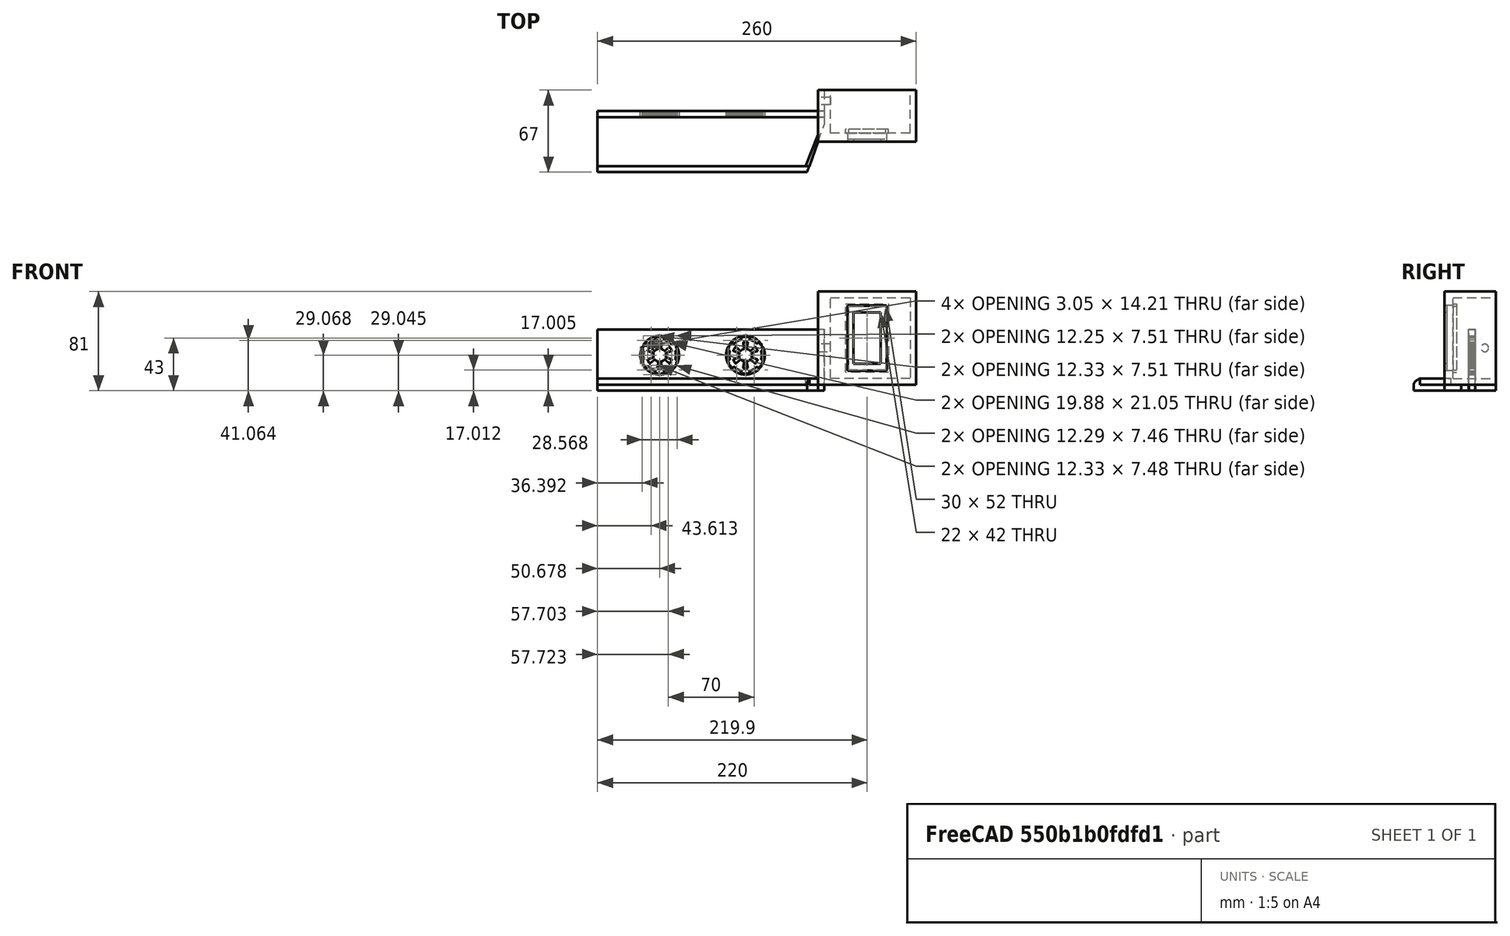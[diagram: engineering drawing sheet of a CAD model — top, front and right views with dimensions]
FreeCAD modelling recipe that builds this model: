
FCSTD DOCUMENT  (FreeCAD 1.0R39109 (Git))
Label: PC Power Button
License: All rights reserved
LicenseURL: https://en.wikipedia.org/wiki/All_rights_reserved
objects: Sketcher::SketchObject×13, PartDesign::Pad×9, PartDesign::Pocket×4, PartDesign::Body×3, Mesh::Feature×1
note: 68 computed .brp shape members not serialized (recipe doc carries the construction recipe); baked Part::Feature solids carry a one-line shape summary decoded from their .brp

FEATURE [Sketcher::SketchObject] Sketch
  ArcFitTolerance = 1e-06
  AttachmentSupport = -> [XZ_Plane]
  FullyConstrained = true
  MakeInternals = false
  MapMode = 5
  Placement = pos=(0,0,0) rot=(1,0,0;1.5708rad)
  sketch-geometry (8):
    g0: LineSegment StartX=-40 StartY=0 StartZ=0 EndX=40 EndY=0 EndZ=0
    g1: LineSegment StartX=40 StartY=0 StartZ=0 EndX=40 EndY=76 EndZ=0
    g2: LineSegment StartX=40 StartY=76 StartZ=0 EndX=-40 EndY=76 EndZ=0
    g3: LineSegment StartX=-40 StartY=76 StartZ=0 EndX=-40 EndY=0 EndZ=0
    g4: LineSegment StartX=-16.1 StartY=64.75 StartZ=0 EndX=-16.1 EndY=11.25 EndZ=0
    g5: LineSegment StartX=-16.1 StartY=11.25 StartZ=0 EndX=15.9 EndY=11.25 EndZ=0
    g6: LineSegment StartX=15.9 StartY=11.25 StartZ=0 EndX=15.9 EndY=64.75 EndZ=0
    g7: LineSegment StartX=15.9 StartY=64.75 StartZ=0 EndX=-16.1 EndY=64.75 EndZ=0
  constraints (24):
    c: Coincident(g0,g1)
    c: Coincident(g1,g2)
    c: Coincident(g2,g3)
    c: Coincident(g3,g0)
    c: Horizontal(g0)
    c: Horizontal(g2)
    c: Vertical(g1)
    c: Vertical(g3)
    c: Distance(g1,g3) = 80
    c: Distance(g0,g2) = 76
    c: PointOnObject(g0,g-1)
    c: Distance(g0,g-2) = 40
    c: Coincident(g4,g5)
    c: Coincident(g5,g6)
    c: Coincident(g6,g7)
    c: Coincident(g7,g4)
    c: Vertical(g4)
    c: Vertical(g6)
    c: Horizontal(g5)
    c: Horizontal(g7)
    c: Distance(g4,g6) = 32
    c: Distance(g5,g7) = 53.5
    c: Distance(g0,g5) = 11.25
    c: Distance(g4,g-2) = 16.1
FEATURE [PartDesign::Pad] Pad
  Direction = (0,-1,2e-16)
  Length = 7
  Length2 = 10
  Placement = pos=(0,0,0) rot=(1,0,0;1.5708rad)
  Profile = -> Sketch
  ReferenceAxis = -> Sketch [N_Axis]
  Refine = true
  Suppressed = false
  Type = 0
FEATURE [Sketcher::SketchObject] Sketch001
  ArcFitTolerance = 1e-06
  AttachmentSupport = -> [Pad]
  FullyConstrained = true
  MakeInternals = false
  MapMode = 5
  Placement = pos=(0,8.4e-15,0) rot=(-1,0,0;1.5708rad)
  sketch-geometry (8):
    g0: LineSegment StartX=-40 StartY=0 StartZ=0 EndX=-40 EndY=-76 EndZ=0
    g1: LineSegment StartX=-40 StartY=-76 StartZ=0 EndX=40 EndY=-76 EndZ=0
    g2: LineSegment StartX=40 StartY=-76 StartZ=0 EndX=40 EndY=0 EndZ=0
    g3: LineSegment StartX=40 StartY=0 StartZ=0 EndX=-40 EndY=0 EndZ=0
    g4: LineSegment StartX=-30 StartY=-5 StartZ=0 EndX=-30 EndY=-71 EndZ=0
    g5: LineSegment StartX=-30 StartY=-71 StartZ=0 EndX=35 EndY=-71 EndZ=0
    g6: LineSegment StartX=35 StartY=-71 StartZ=0 EndX=35 EndY=-5 EndZ=0
    g7: LineSegment StartX=35 StartY=-5 StartZ=0 EndX=-30 EndY=-5 EndZ=0
  constraints (24):
    c: Coincident(g0,g1)
    c: Coincident(g1,g2)
    c: Coincident(g2,g3)
    c: Coincident(g3,g0)
    c: Vertical(g0)
    c: Vertical(g2)
    c: Horizontal(g1)
    c: Horizontal(g3)
    c: Distance(g0,g2) = 80
    c: Distance(g1,g3) = 76
    c: PointOnObject(g0,g-1)
    c: Coincident(g4,g5)
    c: Coincident(g5,g6)
    c: Coincident(g6,g7)
    c: Coincident(g7,g4)
    c: Vertical(g4)
    c: Vertical(g6)
    c: Horizontal(g5)
    c: Horizontal(g7)
    c: Distance(g4,g6) = 65
    c: Distance(g5,g7) = 66
    c: Distance(g5,g1) = 5
    c: Distance(g5,g2) = 5
    c: Distance(g4,g-2) = 30
FEATURE [PartDesign::Pad] Pad001
  BaseFeature = -> Pad
  Direction = (0,1,2e-16)
  Length = 35
  Length2 = 10
  Placement = pos=(0,0,0) rot=(1,0,0;1.5708rad)
  Profile = -> Sketch001
  ReferenceAxis = -> Sketch001 [N_Axis]
  Refine = true
  Suppressed = false
  Type = 0
FEATURE [Mesh::Feature] pc_power_button  label="bticino power button socket"
  Placement = pos=(0,-9.5,-0.5) rot=(0,0,1;0rad)
FEATURE [Sketcher::SketchObject] Sketch002
  ArcFitTolerance = 1e-06
  AttachmentSupport = -> [XZ_Plane001]
  FullyConstrained = true
  MakeInternals = false
  MapMode = 5
  Placement = pos=(0,0,0) rot=(1,0,0;1.5708rad)
  sketch-geometry (8):
    g0: LineSegment StartX=-15.75 StartY=24.5 StartZ=0 EndX=-15.75 EndY=-28.5 EndZ=0
    g1: LineSegment StartX=-15.75 StartY=-28.5 StartZ=0 EndX=15.75 EndY=-28.5 EndZ=0
    g2: LineSegment StartX=15.75 StartY=-28.5 StartZ=0 EndX=15.75 EndY=24.5 EndZ=0
    g3: LineSegment StartX=15.75 StartY=24.5 StartZ=0 EndX=-15.75 EndY=24.5 EndZ=0
    g4: LineSegment StartX=-11 StartY=19 StartZ=0 EndX=-11 EndY=-23 EndZ=0
    g5: LineSegment StartX=-11 StartY=-23 StartZ=0 EndX=11 EndY=-23 EndZ=0
    g6: LineSegment StartX=11 StartY=-23 StartZ=0 EndX=11 EndY=19 EndZ=0
    g7: LineSegment StartX=11 StartY=19 StartZ=0 EndX=-11 EndY=19 EndZ=0
  constraints (24):
    c: Coincident(g0,g1)
    c: Coincident(g1,g2)
    c: Coincident(g2,g3)
    c: Coincident(g3,g0)
    c: Vertical(g0)
    c: Vertical(g2)
    c: Horizontal(g1)
    c: Horizontal(g3)
    c: Distance(g0,g2) = 31.5
    c: Distance(g1,g3) = 53
    c: DistanceY(g-1,g0) = 24.5
    c: Coincident(g4,g5)
    c: Coincident(g5,g6)
    c: Coincident(g6,g7)
    c: Coincident(g7,g4)
    c: Vertical(g4)
    c: Vertical(g6)
    c: Horizontal(g5)
    c: Horizontal(g7)
    c: Distance(g4,g6) = 22
    c: Distance(g5,g7) = 42
    c: Distance(g4,g-2) = 11
    c: Distance(g0,g-2) = 15.75
    c: Distance(g4,g-1) = 19
FEATURE [PartDesign::Pad] Pad002
  Direction = (0,-1,2e-16)
  Length = 2
  Length2 = 10
  Placement = pos=(0,0,0) rot=(1,0,0;1.5708rad)
  Profile = -> Sketch002
  ReferenceAxis = -> Sketch002 [N_Axis]
  Refine = true
  Suppressed = false
  Type = 0
FEATURE [PartDesign::Body] Body001  label="Button cover"
  AllowCompound = false
  Group = -> [Sketch002,Pad002]
  Origin = -> Origin001
  Placement = pos=(-0.1,-48,40) rot=(0,0,1;0rad)
  Tip = -> Pad002
FEATURE [Sketcher::SketchObject] Sketch003
  ArcFitTolerance = 1e-06
  AttachmentSupport = -> [XY_Plane002]
  FullyConstrained = true
  MakeInternals = false
  MapMode = 5
  sketch-geometry (5):
    g0: LineSegment StartX=0 StartY=0 StartZ=0 EndX=-9.09925 EndY=-25 EndZ=0
    g1: LineSegment StartX=0 StartY=0 StartZ=0 EndX=0 EndY=25 EndZ=0
    g2: LineSegment StartX=0 StartY=25 StartZ=0 EndX=-180 EndY=25 EndZ=0
    g3: LineSegment StartX=-180 StartY=25 StartZ=0 EndX=-180 EndY=-25 EndZ=0
    g4: LineSegment StartX=-180 StartY=-25 StartZ=0 EndX=-9.09925 EndY=-25 EndZ=0
  constraints (14):
    c: Angle(g-1,g0) = -1.91986
    c: Coincident(g0,g-1)
    c: Coincident(g1,g0)
    c: PointOnObject(g1,g-2)
    c: Distance(g2) = 180
    c: Coincident(g2,g1)
    c: Horizontal(g2)
    c: Distance(g3) = 50
    c: Coincident(g3,g2)
    c: Vertical(g3)
    c: Parallel(g4,g-1)
    c: Coincident(g3,g4)
    c: Coincident(g0,g4)
    c: DistanceY(g-1,g2) = 25
FEATURE [PartDesign::Pad] Pad003
  Direction = (0,0,1)
  Length = 5
  Length2 = 10
  Profile = -> Sketch003
  ReferenceAxis = -> Sketch003 [N_Axis]
  Refine = true
  Suppressed = false
  Type = 0
FEATURE [Sketcher::SketchObject] Sketch004
  ArcFitTolerance = 1e-06
  AttachmentSupport = -> [Pad003]
  FullyConstrained = true
  MakeInternals = false
  MapMode = 5
  Placement = pos=(-180,0,0) rot=(0.57735,-0.57735,-0.57735;2.0944rad)
  sketch-geometry (9):
    g0: LineSegment StartX=25 StartY=5 StartZ=0 EndX=20 EndY=5 EndZ=0
    g1: LineSegment StartX=20 StartY=5 StartZ=0 EndX=20 EndY=10 EndZ=0
    g2-g5: Circle [constr] x4 (B-spline internal-alignment scaffolding for g6; pole/knot coordinates omitted)
    g6: BSplineCurve PolesCount=4 KnotsCount=2 Degree=3 IsPeriodic=0
    g7: GeomPoint [constr] X=25 Y=5 Z=0
    g8: GeomPoint [constr] X=20 Y=10 Z=0
  constraints (20):
    c: Distance(g0) = 5
    c: Horizontal(g0)
    c: Distance(g0,g-1) = 5
    c: DistanceX(g-1,g0) = 20
    c: Distance(g1) = 5
    c: Parallel(g1,g-2)
    c: Coincident(g0,g1)
    c: Weight(g2) = 1
    c: Equal(g2,g3)
    c: Equal(g2,g4)
    c: Equal(g2,g5)
    c: InternalAlignment(g2-g5 -> g6) x4
    c: InternalAlignment(g7,g6)
    c: InternalAlignment(g8,g6)
    c: Coincident(g2,g0)
    c: Coincident(g1,g6)
    c: DistanceX(g1,g4) = 1.4
    c: Distance(g4,g-1) = 23.3
    c: Distance(g3,g-1) = 26
    c: DistanceX(g4,g3) = 3.4
FEATURE [PartDesign::Pad] Pad004
  BaseFeature = -> Pad003
  Direction = (-1,0,0)
  Length = 10
  Length2 = 10
  Profile = -> Sketch004
  ReferenceAxis = -> Sketch004 [N_Axis]
  Refine = true
  Reversed = true
  Suppressed = false
  Type = 3
  UpToFace = -> Pad003 [Face1]
FEATURE [Sketcher::SketchObject] Sketch005
  ArcFitTolerance = 1e-06
  AttachmentSupport = -> [Pad001]
  FullyConstrained = true
  MakeInternals = false
  MapMode = 5
  Placement = pos=(0,0,1.6e-15) rot=(1,0,0;3.14159rad)
  sketch-geometry (4):
    g0: LineSegment StartX=-40 StartY=-35 StartZ=0 EndX=-40 EndY=7 EndZ=0
    g1: LineSegment StartX=-40 StartY=-35 StartZ=0 EndX=-35 EndY=-35 EndZ=0
    g2: LineSegment StartX=-35 StartY=-35 StartZ=0 EndX=-35 EndY=-6.75 EndZ=0
    g3: LineSegment StartX=-40 StartY=7 StartZ=0 EndX=-35 EndY=-6.75 EndZ=0
  constraints (12):
    c: Distance(g0) = 42
    c: Vertical(g0)
    c: Distance(g1) = 5
    c: Coincident(g1,g0)
    c: Horizontal(g1)
    c: Distance(g2) = 28.25
    c: Coincident(g2,g1)
    c: Vertical(g2)
    c: Coincident(g2,g3)
    c: Coincident(g0,g3)
    c: DistanceX(g0,g-1) = 40
    c: Distance(g0,g-1) = 7
FEATURE [PartDesign::Pad] Pad005
  BaseFeature = -> Pad001
  Direction = (0,0,-1)
  Length = 5
  Length2 = 10
  Placement = pos=(0,0,0) rot=(1,0,0;1.5708rad)
  Profile = -> Sketch005
  ReferenceAxis = -> Sketch005 [N_Axis]
  Refine = true
  Suppressed = false
  Type = 0
FEATURE [Sketcher::SketchObject] Sketch007
  ArcFitTolerance = 1e-06
  AttachmentSupport = -> [Pad004]
  FullyConstrained = true
  MakeInternals = false
  MapMode = 5
  Placement = pos=(0,0,5) rot=(0,0,1;0rad)
  sketch-geometry (4):
    g0: LineSegment StartX=-7.25 StartY=-20 StartZ=0 EndX=-10.25 EndY=-20 EndZ=0
    g1: LineSegment StartX=-10.25 StartY=-20 StartZ=0 EndX=0 EndY=5.45 EndZ=0
    g2: LineSegment StartX=0 StartY=5.45 StartZ=0 EndX=-9e-16 EndY=0 EndZ=0
    g3: LineSegment StartX=-7.25 StartY=-20 StartZ=0 EndX=-9e-16 EndY=0 EndZ=0
  constraints (11):
    c: Distance(g0) = 3
    c: Horizontal(g0)
    c: Distance(g0,g-1) = 20
    c: Coincident(g1,g0)
    c: PointOnObject(g1,g-2)
    c: Coincident(g1,g2)
    c: Coincident(g-1,g2)
    c: Distance(g0,g-2) = 7.25
    c: DistanceY(g-1,g1) = 5.45
    c: Coincident(g3,g0)
    c: Coincident(g3,g2)
FEATURE [PartDesign::Pad] Pad006
  BaseFeature = -> Pad004
  Direction = (0,0,1)
  Length = 5
  Length2 = 10
  Profile = -> Sketch007
  ReferenceAxis = -> Sketch007 [N_Axis]
  Refine = true
  Suppressed = false
  Type = 0
FEATURE [Sketcher::SketchObject] Sketch008
  ArcFitTolerance = 1e-06
  AttachmentSupport = -> [Pad005]
  FullyConstrained = true
  MakeInternals = false
  MapMode = 5
  Placement = pos=(-40,0,0) rot=(0.707107,0,-0.707107;3.14159rad)
  sketch-geometry (4):
    g0: LineSegment StartX=5 StartY=-18.15 StartZ=0 EndX=5 EndY=-12.85 EndZ=0
    g1: LineSegment StartX=5 StartY=-12.85 StartZ=0 EndX=-45.2 EndY=-12.85 EndZ=0
    g2: LineSegment StartX=-45.2 StartY=-12.85 StartZ=0 EndX=-45.2 EndY=-18.15 EndZ=0
    g3: LineSegment StartX=-45.2 StartY=-18.15 StartZ=0 EndX=5 EndY=-18.15 EndZ=0
  constraints (12):
    c: Coincident(g0,g1)
    c: Coincident(g1,g2)
    c: Coincident(g2,g3)
    c: Coincident(g3,g0)
    c: Vertical(g0)
    c: Vertical(g2)
    c: Horizontal(g1)
    c: Horizontal(g3)
    c: Distance(g0,g2) = 50.2
    c: Distance(g1,g3) = 5.3
    c: Distance(g0,g-2) = 5
    c: Distance(g0,g-1) = 12.85
FEATURE [PartDesign::Pocket] Pocket
  BaseFeature = -> Pad005
  Direction = (1,0,2e-16)
  Length = 5
  Length2 = 5
  Placement = pos=(0,0,0) rot=(1,0,0;1.5708rad)
  Profile = -> Sketch008
  ReferenceAxis = -> Sketch008 [N_Axis]
  Refine = true
  Suppressed = false
  Type = 0
FEATURE [Sketcher::SketchObject] Sketch009
  ArcFitTolerance = 1e-06
  AttachmentSupport = -> [Pad006]
  FullyConstrained = true
  MakeInternals = false
  MapMode = 5
  Placement = pos=(0,0,0) rot=(1,0,0;3.14159rad)
  sketch-geometry (4):
    g0: LineSegment StartX=-180 StartY=-20 StartZ=0 EndX=-180 EndY=-25 EndZ=0
    g1: LineSegment StartX=-180 StartY=-25 StartZ=0 EndX=5 EndY=-25 EndZ=0
    g2: LineSegment StartX=5 StartY=-25 StartZ=0 EndX=5 EndY=-20 EndZ=0
    g3: LineSegment StartX=5 StartY=-20 StartZ=0 EndX=-180 EndY=-20 EndZ=0
  constraints (12):
    c: Coincident(g0,g1)
    c: Coincident(g1,g2)
    c: Coincident(g2,g3)
    c: Coincident(g3,g0)
    c: Vertical(g0)
    c: Vertical(g2)
    c: Horizontal(g1)
    c: Horizontal(g3)
    c: Distance(g0,g2) = 185
    c: Distance(g1,g3) = 5
    c: Distance(g0,g-1) = 20
    c: Distance(g2,g-2) = 5
FEATURE [PartDesign::Pad] Pad007
  BaseFeature = -> Pad006
  Direction = (0,0,-1)
  Length = 50
  Length2 = 10
  Profile = -> Sketch009
  ReferenceAxis = -> Sketch009 [N_Axis]
  Refine = true
  Reversed = true
  Suppressed = false
  Type = 0
FEATURE [Sketcher::SketchObject] Sketch010
  ArcFitTolerance = 1e-06
  AttachmentSupport = -> [Pad007]
  FullyConstrained = false
  MakeInternals = false
  MapMode = 5
  Placement = pos=(0,20,0) rot=(1,0,0;1.5708rad)
  sketch-geometry (176):
    g0: BSplineCurve PolesCount=4 KnotsCount=2 Degree=3 IsPeriodic=0
    g1: BSplineCurve PolesCount=4 KnotsCount=2 Degree=3 IsPeriodic=0
    g2: BSplineCurve PolesCount=4 KnotsCount=2 Degree=3 IsPeriodic=0
    g3: BSplineCurve PolesCount=4 KnotsCount=2 Degree=3 IsPeriodic=0
    g4: BSplineCurve PolesCount=4 KnotsCount=2 Degree=3 IsPeriodic=0
    g5: BSplineCurve PolesCount=4 KnotsCount=2 Degree=3 IsPeriodic=0
    g6: BSplineCurve PolesCount=4 KnotsCount=2 Degree=3 IsPeriodic=0
    g7: BSplineCurve PolesCount=4 KnotsCount=2 Degree=3 IsPeriodic=0
    g8: BSplineCurve PolesCount=4 KnotsCount=2 Degree=3 IsPeriodic=0
    g9: BSplineCurve PolesCount=4 KnotsCount=2 Degree=3 IsPeriodic=0
    g10: BSplineCurve PolesCount=4 KnotsCount=2 Degree=3 IsPeriodic=0
    g11: BSplineCurve PolesCount=4 KnotsCount=2 Degree=3 IsPeriodic=0
    g12: BSplineCurve PolesCount=4 KnotsCount=2 Degree=3 IsPeriodic=0
    g13: BSplineCurve PolesCount=4 KnotsCount=2 Degree=3 IsPeriodic=0
    g14: BSplineCurve PolesCount=4 KnotsCount=2 Degree=3 IsPeriodic=0
    g15: BSplineCurve PolesCount=4 KnotsCount=2 Degree=3 IsPeriodic=0
    g16: BSplineCurve PolesCount=4 KnotsCount=2 Degree=3 IsPeriodic=0
    g17: BSplineCurve PolesCount=4 KnotsCount=2 Degree=3 IsPeriodic=0
    g18: BSplineCurve PolesCount=4 KnotsCount=2 Degree=3 IsPeriodic=0
    g19: BSplineCurve PolesCount=4 KnotsCount=2 Degree=3 IsPeriodic=0
    g20: BSplineCurve PolesCount=4 KnotsCount=2 Degree=3 IsPeriodic=0
    g21: BSplineCurve PolesCount=4 KnotsCount=2 Degree=3 IsPeriodic=0
    g22: BSplineCurve PolesCount=4 KnotsCount=2 Degree=3 IsPeriodic=0
    g23: BSplineCurve PolesCount=4 KnotsCount=2 Degree=3 IsPeriodic=0
    g24: BSplineCurve PolesCount=4 KnotsCount=2 Degree=3 IsPeriodic=0
    g25: BSplineCurve PolesCount=4 KnotsCount=2 Degree=3 IsPeriodic=0
    g26: BSplineCurve PolesCount=4 KnotsCount=2 Degree=3 IsPeriodic=0
    g27: BSplineCurve PolesCount=4 KnotsCount=2 Degree=3 IsPeriodic=0
    g28: BSplineCurve PolesCount=4 KnotsCount=2 Degree=3 IsPeriodic=0
    g29: BSplineCurve PolesCount=4 KnotsCount=2 Degree=3 IsPeriodic=0
    g30: BSplineCurve PolesCount=4 KnotsCount=2 Degree=3 IsPeriodic=0
    g31: BSplineCurve PolesCount=4 KnotsCount=2 Degree=3 IsPeriodic=0
    g32: BSplineCurve PolesCount=4 KnotsCount=2 Degree=3 IsPeriodic=0
    g33: BSplineCurve PolesCount=4 KnotsCount=2 Degree=3 IsPeriodic=0
    g34: BSplineCurve PolesCount=4 KnotsCount=2 Degree=3 IsPeriodic=0
    g35: BSplineCurve PolesCount=4 KnotsCount=2 Degree=3 IsPeriodic=0
    g36: BSplineCurve PolesCount=4 KnotsCount=2 Degree=3 IsPeriodic=0
    g37: BSplineCurve PolesCount=4 KnotsCount=2 Degree=3 IsPeriodic=0
    g38: BSplineCurve PolesCount=4 KnotsCount=2 Degree=3 IsPeriodic=0
    g39: BSplineCurve PolesCount=4 KnotsCount=2 Degree=3 IsPeriodic=0
    g40: BSplineCurve PolesCount=4 KnotsCount=2 Degree=3 IsPeriodic=0
    g41: BSplineCurve PolesCount=4 KnotsCount=2 Degree=3 IsPeriodic=0
    g42: BSplineCurve PolesCount=4 KnotsCount=2 Degree=3 IsPeriodic=0
    g43: BSplineCurve PolesCount=4 KnotsCount=2 Degree=3 IsPeriodic=0
    g44: BSplineCurve PolesCount=4 KnotsCount=2 Degree=3 IsPeriodic=0
    g45: BSplineCurve PolesCount=4 KnotsCount=2 Degree=3 IsPeriodic=0
    g46: BSplineCurve PolesCount=4 KnotsCount=2 Degree=3 IsPeriodic=0
    g47: BSplineCurve PolesCount=4 KnotsCount=2 Degree=3 IsPeriodic=0
    g48: BSplineCurve PolesCount=4 KnotsCount=2 Degree=3 IsPeriodic=0
    g49: BSplineCurve PolesCount=4 KnotsCount=2 Degree=3 IsPeriodic=0
    g50: BSplineCurve PolesCount=4 KnotsCount=2 Degree=3 IsPeriodic=0
    g51: BSplineCurve PolesCount=4 KnotsCount=2 Degree=3 IsPeriodic=0
    g52: BSplineCurve PolesCount=4 KnotsCount=2 Degree=3 IsPeriodic=0
    g53: BSplineCurve PolesCount=4 KnotsCount=2 Degree=3 IsPeriodic=0
    g54: BSplineCurve PolesCount=4 KnotsCount=2 Degree=3 IsPeriodic=0
    g55: BSplineCurve PolesCount=4 KnotsCount=2 Degree=3 IsPeriodic=0
    g56: BSplineCurve PolesCount=4 KnotsCount=2 Degree=3 IsPeriodic=0
    g57: BSplineCurve PolesCount=4 KnotsCount=2 Degree=3 IsPeriodic=0
    g58: BSplineCurve PolesCount=4 KnotsCount=2 Degree=3 IsPeriodic=0
    g59: BSplineCurve PolesCount=4 KnotsCount=2 Degree=3 IsPeriodic=0
    g60: BSplineCurve PolesCount=4 KnotsCount=2 Degree=3 IsPeriodic=0
    g61: BSplineCurve PolesCount=4 KnotsCount=2 Degree=3 IsPeriodic=0
    g62: BSplineCurve PolesCount=4 KnotsCount=2 Degree=3 IsPeriodic=0
    g63: BSplineCurve PolesCount=4 KnotsCount=2 Degree=3 IsPeriodic=0
    g64: BSplineCurve PolesCount=4 KnotsCount=2 Degree=3 IsPeriodic=0
    g65: BSplineCurve PolesCount=4 KnotsCount=2 Degree=3 IsPeriodic=0
    g66: BSplineCurve PolesCount=4 KnotsCount=2 Degree=3 IsPeriodic=0
    g67: BSplineCurve PolesCount=4 KnotsCount=2 Degree=3 IsPeriodic=0
    g68: BSplineCurve PolesCount=4 KnotsCount=2 Degree=3 IsPeriodic=0
    g69: BSplineCurve PolesCount=4 KnotsCount=2 Degree=3 IsPeriodic=0
    g70: BSplineCurve PolesCount=4 KnotsCount=2 Degree=3 IsPeriodic=0
    g71: BSplineCurve PolesCount=4 KnotsCount=2 Degree=3 IsPeriodic=0
    g72: BSplineCurve PolesCount=4 KnotsCount=2 Degree=3 IsPeriodic=0
    g73: BSplineCurve PolesCount=4 KnotsCount=2 Degree=3 IsPeriodic=0
    g74: BSplineCurve PolesCount=4 KnotsCount=2 Degree=3 IsPeriodic=0
    g75: BSplineCurve PolesCount=4 KnotsCount=2 Degree=3 IsPeriodic=0
    g76: BSplineCurve PolesCount=4 KnotsCount=2 Degree=3 IsPeriodic=0
    g77: BSplineCurve PolesCount=4 KnotsCount=2 Degree=3 IsPeriodic=0
    g78: BSplineCurve PolesCount=4 KnotsCount=2 Degree=3 IsPeriodic=0
    g79: BSplineCurve PolesCount=4 KnotsCount=2 Degree=3 IsPeriodic=0
    g80: BSplineCurve PolesCount=4 KnotsCount=2 Degree=3 IsPeriodic=0
    g81: BSplineCurve PolesCount=4 KnotsCount=2 Degree=3 IsPeriodic=0
    g82: BSplineCurve PolesCount=4 KnotsCount=2 Degree=3 IsPeriodic=0
    g83: BSplineCurve PolesCount=4 KnotsCount=2 Degree=3 IsPeriodic=0
    g84: BSplineCurve PolesCount=4 KnotsCount=2 Degree=3 IsPeriodic=0
    g85: BSplineCurve PolesCount=4 KnotsCount=2 Degree=3 IsPeriodic=0
    g86: BSplineCurve PolesCount=4 KnotsCount=2 Degree=3 IsPeriodic=0
    g87: BSplineCurve PolesCount=4 KnotsCount=2 Degree=3 IsPeriodic=0
    g88: BSplineCurve PolesCount=4 KnotsCount=2 Degree=3 IsPeriodic=0
    g89: BSplineCurve PolesCount=4 KnotsCount=2 Degree=3 IsPeriodic=0
    g90: BSplineCurve PolesCount=4 KnotsCount=2 Degree=3 IsPeriodic=0
    g91: BSplineCurve PolesCount=4 KnotsCount=2 Degree=3 IsPeriodic=0
    g92: BSplineCurve PolesCount=4 KnotsCount=2 Degree=3 IsPeriodic=0
    g93: BSplineCurve PolesCount=4 KnotsCount=2 Degree=3 IsPeriodic=0
    g94: BSplineCurve PolesCount=4 KnotsCount=2 Degree=3 IsPeriodic=0
    g95: BSplineCurve PolesCount=4 KnotsCount=2 Degree=3 IsPeriodic=0
    g96: BSplineCurve PolesCount=4 KnotsCount=2 Degree=3 IsPeriodic=0
    g97: BSplineCurve PolesCount=4 KnotsCount=2 Degree=3 IsPeriodic=0
    g98: BSplineCurve PolesCount=4 KnotsCount=2 Degree=3 IsPeriodic=0
    g99: BSplineCurve PolesCount=4 KnotsCount=2 Degree=3 IsPeriodic=0
    g100: BSplineCurve PolesCount=4 KnotsCount=2 Degree=3 IsPeriodic=0
    g101: BSplineCurve PolesCount=4 KnotsCount=2 Degree=3 IsPeriodic=0
    g102: BSplineCurve PolesCount=4 KnotsCount=2 Degree=3 IsPeriodic=0
    g103: BSplineCurve PolesCount=4 KnotsCount=2 Degree=3 IsPeriodic=0
    g104: BSplineCurve PolesCount=4 KnotsCount=2 Degree=3 IsPeriodic=0
    g105: BSplineCurve PolesCount=4 KnotsCount=2 Degree=3 IsPeriodic=0
    g106: BSplineCurve PolesCount=4 KnotsCount=2 Degree=3 IsPeriodic=0
    g107: BSplineCurve PolesCount=4 KnotsCount=2 Degree=3 IsPeriodic=0
    g108: BSplineCurve PolesCount=4 KnotsCount=2 Degree=3 IsPeriodic=0
    g109: BSplineCurve PolesCount=4 KnotsCount=2 Degree=3 IsPeriodic=0
    g110: BSplineCurve PolesCount=4 KnotsCount=2 Degree=3 IsPeriodic=0
    g111: BSplineCurve PolesCount=4 KnotsCount=2 Degree=3 IsPeriodic=0
    g112: BSplineCurve PolesCount=4 KnotsCount=2 Degree=3 IsPeriodic=0
    g113: BSplineCurve PolesCount=4 KnotsCount=2 Degree=3 IsPeriodic=0
    g114: BSplineCurve PolesCount=4 KnotsCount=2 Degree=3 IsPeriodic=0
    g115: BSplineCurve PolesCount=4 KnotsCount=2 Degree=3 IsPeriodic=0
    g116: BSplineCurve PolesCount=4 KnotsCount=2 Degree=3 IsPeriodic=0
    g117: BSplineCurve PolesCount=4 KnotsCount=2 Degree=3 IsPeriodic=0
    g118: BSplineCurve PolesCount=4 KnotsCount=2 Degree=3 IsPeriodic=0
    g119: BSplineCurve PolesCount=4 KnotsCount=2 Degree=3 IsPeriodic=0
    g120: BSplineCurve PolesCount=4 KnotsCount=2 Degree=3 IsPeriodic=0
    g121: BSplineCurve PolesCount=4 KnotsCount=2 Degree=3 IsPeriodic=0
    g122: BSplineCurve PolesCount=4 KnotsCount=2 Degree=3 IsPeriodic=0
    g123: BSplineCurve PolesCount=4 KnotsCount=2 Degree=3 IsPeriodic=0
    g124: BSplineCurve PolesCount=4 KnotsCount=2 Degree=3 IsPeriodic=0
    g125: BSplineCurve PolesCount=4 KnotsCount=2 Degree=3 IsPeriodic=0
    g126: BSplineCurve PolesCount=4 KnotsCount=2 Degree=3 IsPeriodic=0
    g127: BSplineCurve PolesCount=4 KnotsCount=2 Degree=3 IsPeriodic=0
    g128: BSplineCurve PolesCount=4 KnotsCount=2 Degree=3 IsPeriodic=0
    g129: BSplineCurve PolesCount=4 KnotsCount=2 Degree=3 IsPeriodic=0
    g130: BSplineCurve PolesCount=4 KnotsCount=2 Degree=3 IsPeriodic=0
    g131: BSplineCurve PolesCount=4 KnotsCount=2 Degree=3 IsPeriodic=0
    g132: BSplineCurve PolesCount=4 KnotsCount=2 Degree=3 IsPeriodic=0
    g133: BSplineCurve PolesCount=4 KnotsCount=2 Degree=3 IsPeriodic=0
    g134: BSplineCurve PolesCount=4 KnotsCount=2 Degree=3 IsPeriodic=0
    g135: BSplineCurve PolesCount=4 KnotsCount=2 Degree=3 IsPeriodic=0
    g136: BSplineCurve PolesCount=4 KnotsCount=2 Degree=3 IsPeriodic=0
    g137: BSplineCurve PolesCount=4 KnotsCount=2 Degree=3 IsPeriodic=0
    g138: BSplineCurve PolesCount=4 KnotsCount=2 Degree=3 IsPeriodic=0
    g139: BSplineCurve PolesCount=4 KnotsCount=2 Degree=3 IsPeriodic=0
    g140: BSplineCurve PolesCount=4 KnotsCount=2 Degree=3 IsPeriodic=0
    g141: BSplineCurve PolesCount=4 KnotsCount=2 Degree=3 IsPeriodic=0
    g142: BSplineCurve PolesCount=4 KnotsCount=2 Degree=3 IsPeriodic=0
    g143: BSplineCurve PolesCount=4 KnotsCount=2 Degree=3 IsPeriodic=0
    g144: BSplineCurve PolesCount=4 KnotsCount=2 Degree=3 IsPeriodic=0
    g145: BSplineCurve PolesCount=4 KnotsCount=2 Degree=3 IsPeriodic=0
    g146: BSplineCurve PolesCount=4 KnotsCount=2 Degree=3 IsPeriodic=0
    g147: BSplineCurve PolesCount=4 KnotsCount=2 Degree=3 IsPeriodic=0
    g148: BSplineCurve PolesCount=4 KnotsCount=2 Degree=3 IsPeriodic=0
    g149: BSplineCurve PolesCount=4 KnotsCount=2 Degree=3 IsPeriodic=0
    g150: BSplineCurve PolesCount=4 KnotsCount=2 Degree=3 IsPeriodic=0
    g151: BSplineCurve PolesCount=4 KnotsCount=2 Degree=3 IsPeriodic=0
    g152: BSplineCurve PolesCount=4 KnotsCount=2 Degree=3 IsPeriodic=0
    g153: BSplineCurve PolesCount=4 KnotsCount=2 Degree=3 IsPeriodic=0
    g154: BSplineCurve PolesCount=4 KnotsCount=2 Degree=3 IsPeriodic=0
    g155: BSplineCurve PolesCount=4 KnotsCount=2 Degree=3 IsPeriodic=0
    g156: BSplineCurve PolesCount=4 KnotsCount=2 Degree=3 IsPeriodic=0
    g157: BSplineCurve PolesCount=4 KnotsCount=2 Degree=3 IsPeriodic=0
    g158: BSplineCurve PolesCount=4 KnotsCount=2 Degree=3 IsPeriodic=0
    g159: BSplineCurve PolesCount=4 KnotsCount=2 Degree=3 IsPeriodic=0
    g160: BSplineCurve PolesCount=4 KnotsCount=2 Degree=3 IsPeriodic=0
    g161: BSplineCurve PolesCount=4 KnotsCount=2 Degree=3 IsPeriodic=0
    g162: BSplineCurve PolesCount=4 KnotsCount=2 Degree=3 IsPeriodic=0
    g163: BSplineCurve PolesCount=4 KnotsCount=2 Degree=3 IsPeriodic=0
    g164: BSplineCurve PolesCount=4 KnotsCount=2 Degree=3 IsPeriodic=0
    g165: BSplineCurve PolesCount=4 KnotsCount=2 Degree=3 IsPeriodic=0
    g166: BSplineCurve PolesCount=4 KnotsCount=2 Degree=3 IsPeriodic=0
    g167: BSplineCurve PolesCount=4 KnotsCount=2 Degree=3 IsPeriodic=0
    g168: BSplineCurve PolesCount=4 KnotsCount=2 Degree=3 IsPeriodic=0
    g169: BSplineCurve PolesCount=4 KnotsCount=2 Degree=3 IsPeriodic=0
    g170: BSplineCurve PolesCount=4 KnotsCount=2 Degree=3 IsPeriodic=0
    g171: BSplineCurve PolesCount=4 KnotsCount=2 Degree=3 IsPeriodic=0
    g172: BSplineCurve PolesCount=4 KnotsCount=2 Degree=3 IsPeriodic=0
    g173: BSplineCurve PolesCount=4 KnotsCount=2 Degree=3 IsPeriodic=0
    g174: BSplineCurve PolesCount=4 KnotsCount=2 Degree=3 IsPeriodic=0
    g175: BSplineCurve PolesCount=4 KnotsCount=2 Degree=3 IsPeriodic=0
  constraints (176):
    c: Coincident(g0,g1)
    c: Coincident(g1,g2)
    c: Coincident(g2,g3)
    c: Coincident(g3,g4)
    c: Coincident(g4,g5)
    c: Coincident(g5,g6)
    c: Coincident(g6,g7)
    c: Coincident(g7,g8)
    c: Coincident(g8,g9)
    c: Coincident(g9,g10)
    c: Coincident(g10,g11)
    c: Coincident(g11,g12)
    c: Coincident(g12,g13)
    c: Coincident(g13,g14)
    c: Coincident(g14,g0)
    c: Coincident(g15,g16)
    c: Coincident(g16,g17)
    c: Coincident(g17,g18)
    c: Coincident(g18,g19)
    c: Coincident(g19,g20)
    c: Coincident(g20,g21)
    c: Coincident(g21,g22)
    c: Coincident(g22,g23)
    c: Coincident(g23,g24)
    c: Coincident(g24,g25)
    c: Coincident(g25,g26)
    c: Coincident(g26,g27)
    c: Coincident(g27,g28)
    c: Coincident(g28,g29)
    c: Coincident(g29,g30)
    c: Coincident(g30,g31)
    c: Coincident(g31,g32)
    c: Coincident(g32,g15)
    c: Coincident(g33,g34)
    c: Coincident(g34,g35)
    c: Coincident(g35,g36)
    c: Coincident(g36,g37)
    c: Coincident(g37,g38)
    c: Coincident(g38,g39)
    c: Coincident(g39,g40)
    c: Coincident(g40,g41)
    c: Coincident(g41,g42)
    c: Coincident(g42,g43)
    c: Coincident(g43,g44)
    c: Coincident(g44,g45)
    c: Coincident(g45,g46)
    c: Coincident(g46,g47)
    c: Coincident(g47,g48)
    c: Coincident(g48,g49)
    c: Coincident(g49,g50)
    c: Coincident(g50,g51)
    c: Coincident(g51,g52)
    c: Coincident(g52,g53)
    c: Coincident(g53,g54)
    c: Coincident(g54,g55)
    c: Coincident(g55,g56)
    c: Coincident(g56,g57)
    c: Coincident(g57,g58)
    c: Coincident(g58,g59)
    c: Coincident(g59,g60)
    c: Coincident(g60,g61)
    c: Coincident(g61,g62)
    c: Coincident(g62,g63)
    c: Coincident(g63,g64)
    c: Coincident(g64,g65)
    c: Coincident(g65,g66)
    c: Coincident(g66,g67)
    c: Coincident(g67,g68)
    c: Coincident(g68,g69)
    c: Coincident(g69,g70)
    c: Coincident(g70,g71)
    c: Coincident(g71,g72)
    c: Coincident(g72,g73)
    c: Coincident(g73,g74)
    c: Coincident(g74,g75)
    c: Coincident(g75,g76)
    c: Coincident(g76,g77)
    c: Coincident(g77,g78)
    c: Coincident(g78,g79)
    c: Coincident(g79,g80)
    c: Coincident(g80,g81)
    c: Coincident(g81,g82)
    c: Coincident(g82,g83)
    c: Coincident(g83,g84)
    c: Coincident(g84,g85)
    c: Coincident(g85,g86)
    c: Coincident(g86,g87)
    c: Coincident(g87,g88)
    c: Coincident(g88,g89)
    c: Coincident(g89,g90)
    c: Coincident(g90,g91)
    c: Coincident(g91,g92)
    c: Coincident(g92,g93)
    c: Coincident(g93,g94)
    c: Coincident(g94,g95)
    c: Coincident(g95,g96)
    c: Coincident(g96,g97)
    c: Coincident(g97,g98)
    c: Coincident(g98,g99)
    c: Coincident(g99,g100)
    c: Coincident(g100,g101)
    c: Coincident(g101,g102)
    c: Coincident(g102,g33)
    c: Coincident(g103,g104)
    c: Coincident(g104,g105)
    c: Coincident(g105,g106)
    c: Coincident(g106,g107)
    c: Coincident(g107,g108)
    c: Coincident(g108,g109)
    c: Coincident(g109,g110)
    c: Coincident(g110,g111)
    c: Coincident(g111,g112)
    c: Coincident(g112,g113)
    c: Coincident(g113,g114)
    c: Coincident(g114,g115)
    c: Coincident(g115,g116)
    c: Coincident(g116,g117)
    c: Coincident(g117,g118)
    c: Coincident(g118,g119)
    c: Coincident(g119,g120)
    c: Coincident(g120,g121)
    c: Coincident(g121,g103)
    c: Coincident(g122,g123)
    c: Coincident(g123,g124)
    c: Coincident(g124,g125)
    c: Coincident(g125,g126)
    c: Coincident(g126,g127)
    c: Coincident(g127,g128)
    c: Coincident(g128,g129)
    c: Coincident(g129,g130)
    c: Coincident(g130,g131)
    c: Coincident(g131,g132)
    c: Coincident(g132,g133)
    c: Coincident(g133,g134)
    c: Coincident(g134,g135)
    c: Coincident(g135,g136)
    c: Coincident(g136,g137)
    c: Coincident(g137,g138)
    c: Coincident(g138,g139)
    c: Coincident(g139,g140)
    c: Coincident(g140,g141)
    c: Coincident(g141,g142)
    c: Coincident(g142,g143)
    c: Coincident(g143,g144)
    c: Coincident(g144,g122)
    c: Coincident(g145,g146)
    c: Coincident(g146,g147)
    c: Coincident(g147,g148)
    c: Coincident(g148,g149)
    c: Coincident(g149,g150)
    c: Coincident(g150,g151)
    c: Coincident(g151,g152)
    c: Coincident(g152,g153)
    c: Coincident(g153,g154)
    c: Coincident(g154,g155)
    c: Coincident(g155,g156)
    c: Coincident(g156,g157)
    c: Coincident(g157,g158)
    c: Coincident(g158,g159)
    c: Coincident(g159,g160)
    c: Coincident(g160,g145)
    c: Coincident(g161,g162)
    c: Coincident(g162,g163)
    c: Coincident(g163,g164)
    c: Coincident(g164,g165)
    c: Coincident(g165,g166)
    c: Coincident(g166,g167)
    c: Coincident(g167,g168)
    c: Coincident(g168,g169)
    c: Coincident(g169,g170)
    c: Coincident(g170,g171)
    c: Coincident(g171,g172)
    c: Coincident(g172,g173)
    c: Coincident(g173,g174)
    c: Coincident(g174,g175)
    c: Coincident(g175,g161)
FEATURE [Sketcher::SketchObject] Sketch011
  ArcFitTolerance = 1e-06
  AttachmentOffset = pos=(-70,0,0) rot=(0,0,1;0rad)
  AttachmentSupport = -> [Pad007]
  FullyConstrained = false
  MakeInternals = false
  MapMode = 5
  Placement = pos=(-70,20,0) rot=(1,0,0;1.5708rad)
  sketch-geometry (176):
    g0: BSplineCurve PolesCount=4 KnotsCount=2 Degree=3 IsPeriodic=0
    g1: BSplineCurve PolesCount=4 KnotsCount=2 Degree=3 IsPeriodic=0
    g2: BSplineCurve PolesCount=4 KnotsCount=2 Degree=3 IsPeriodic=0
    g3: BSplineCurve PolesCount=4 KnotsCount=2 Degree=3 IsPeriodic=0
    g4: BSplineCurve PolesCount=4 KnotsCount=2 Degree=3 IsPeriodic=0
    g5: BSplineCurve PolesCount=4 KnotsCount=2 Degree=3 IsPeriodic=0
    g6: BSplineCurve PolesCount=4 KnotsCount=2 Degree=3 IsPeriodic=0
    g7: BSplineCurve PolesCount=4 KnotsCount=2 Degree=3 IsPeriodic=0
    g8: BSplineCurve PolesCount=4 KnotsCount=2 Degree=3 IsPeriodic=0
    g9: BSplineCurve PolesCount=4 KnotsCount=2 Degree=3 IsPeriodic=0
    g10: BSplineCurve PolesCount=4 KnotsCount=2 Degree=3 IsPeriodic=0
    g11: BSplineCurve PolesCount=4 KnotsCount=2 Degree=3 IsPeriodic=0
    g12: BSplineCurve PolesCount=4 KnotsCount=2 Degree=3 IsPeriodic=0
    g13: BSplineCurve PolesCount=4 KnotsCount=2 Degree=3 IsPeriodic=0
    g14: BSplineCurve PolesCount=4 KnotsCount=2 Degree=3 IsPeriodic=0
    g15: BSplineCurve PolesCount=4 KnotsCount=2 Degree=3 IsPeriodic=0
    g16: BSplineCurve PolesCount=4 KnotsCount=2 Degree=3 IsPeriodic=0
    g17: BSplineCurve PolesCount=4 KnotsCount=2 Degree=3 IsPeriodic=0
    g18: BSplineCurve PolesCount=4 KnotsCount=2 Degree=3 IsPeriodic=0
    g19: BSplineCurve PolesCount=4 KnotsCount=2 Degree=3 IsPeriodic=0
    g20: BSplineCurve PolesCount=4 KnotsCount=2 Degree=3 IsPeriodic=0
    g21: BSplineCurve PolesCount=4 KnotsCount=2 Degree=3 IsPeriodic=0
    g22: BSplineCurve PolesCount=4 KnotsCount=2 Degree=3 IsPeriodic=0
    g23: BSplineCurve PolesCount=4 KnotsCount=2 Degree=3 IsPeriodic=0
    g24: BSplineCurve PolesCount=4 KnotsCount=2 Degree=3 IsPeriodic=0
    g25: BSplineCurve PolesCount=4 KnotsCount=2 Degree=3 IsPeriodic=0
    g26: BSplineCurve PolesCount=4 KnotsCount=2 Degree=3 IsPeriodic=0
    g27: BSplineCurve PolesCount=4 KnotsCount=2 Degree=3 IsPeriodic=0
    g28: BSplineCurve PolesCount=4 KnotsCount=2 Degree=3 IsPeriodic=0
    g29: BSplineCurve PolesCount=4 KnotsCount=2 Degree=3 IsPeriodic=0
    g30: BSplineCurve PolesCount=4 KnotsCount=2 Degree=3 IsPeriodic=0
    g31: BSplineCurve PolesCount=4 KnotsCount=2 Degree=3 IsPeriodic=0
    g32: BSplineCurve PolesCount=4 KnotsCount=2 Degree=3 IsPeriodic=0
    g33: BSplineCurve PolesCount=4 KnotsCount=2 Degree=3 IsPeriodic=0
    g34: BSplineCurve PolesCount=4 KnotsCount=2 Degree=3 IsPeriodic=0
    g35: BSplineCurve PolesCount=4 KnotsCount=2 Degree=3 IsPeriodic=0
    g36: BSplineCurve PolesCount=4 KnotsCount=2 Degree=3 IsPeriodic=0
    g37: BSplineCurve PolesCount=4 KnotsCount=2 Degree=3 IsPeriodic=0
    g38: BSplineCurve PolesCount=4 KnotsCount=2 Degree=3 IsPeriodic=0
    g39: BSplineCurve PolesCount=4 KnotsCount=2 Degree=3 IsPeriodic=0
    g40: BSplineCurve PolesCount=4 KnotsCount=2 Degree=3 IsPeriodic=0
    g41: BSplineCurve PolesCount=4 KnotsCount=2 Degree=3 IsPeriodic=0
    g42: BSplineCurve PolesCount=4 KnotsCount=2 Degree=3 IsPeriodic=0
    g43: BSplineCurve PolesCount=4 KnotsCount=2 Degree=3 IsPeriodic=0
    g44: BSplineCurve PolesCount=4 KnotsCount=2 Degree=3 IsPeriodic=0
    g45: BSplineCurve PolesCount=4 KnotsCount=2 Degree=3 IsPeriodic=0
    g46: BSplineCurve PolesCount=4 KnotsCount=2 Degree=3 IsPeriodic=0
    g47: BSplineCurve PolesCount=4 KnotsCount=2 Degree=3 IsPeriodic=0
    g48: BSplineCurve PolesCount=4 KnotsCount=2 Degree=3 IsPeriodic=0
    g49: BSplineCurve PolesCount=4 KnotsCount=2 Degree=3 IsPeriodic=0
    g50: BSplineCurve PolesCount=4 KnotsCount=2 Degree=3 IsPeriodic=0
    g51: BSplineCurve PolesCount=4 KnotsCount=2 Degree=3 IsPeriodic=0
    g52: BSplineCurve PolesCount=4 KnotsCount=2 Degree=3 IsPeriodic=0
    g53: BSplineCurve PolesCount=4 KnotsCount=2 Degree=3 IsPeriodic=0
    g54: BSplineCurve PolesCount=4 KnotsCount=2 Degree=3 IsPeriodic=0
    g55: BSplineCurve PolesCount=4 KnotsCount=2 Degree=3 IsPeriodic=0
    g56: BSplineCurve PolesCount=4 KnotsCount=2 Degree=3 IsPeriodic=0
    g57: BSplineCurve PolesCount=4 KnotsCount=2 Degree=3 IsPeriodic=0
    g58: BSplineCurve PolesCount=4 KnotsCount=2 Degree=3 IsPeriodic=0
    g59: BSplineCurve PolesCount=4 KnotsCount=2 Degree=3 IsPeriodic=0
    g60: BSplineCurve PolesCount=4 KnotsCount=2 Degree=3 IsPeriodic=0
    g61: BSplineCurve PolesCount=4 KnotsCount=2 Degree=3 IsPeriodic=0
    g62: BSplineCurve PolesCount=4 KnotsCount=2 Degree=3 IsPeriodic=0
    g63: BSplineCurve PolesCount=4 KnotsCount=2 Degree=3 IsPeriodic=0
    g64: BSplineCurve PolesCount=4 KnotsCount=2 Degree=3 IsPeriodic=0
    g65: BSplineCurve PolesCount=4 KnotsCount=2 Degree=3 IsPeriodic=0
    g66: BSplineCurve PolesCount=4 KnotsCount=2 Degree=3 IsPeriodic=0
    g67: BSplineCurve PolesCount=4 KnotsCount=2 Degree=3 IsPeriodic=0
    g68: BSplineCurve PolesCount=4 KnotsCount=2 Degree=3 IsPeriodic=0
    g69: BSplineCurve PolesCount=4 KnotsCount=2 Degree=3 IsPeriodic=0
    g70: BSplineCurve PolesCount=4 KnotsCount=2 Degree=3 IsPeriodic=0
    g71: BSplineCurve PolesCount=4 KnotsCount=2 Degree=3 IsPeriodic=0
    g72: BSplineCurve PolesCount=4 KnotsCount=2 Degree=3 IsPeriodic=0
    g73: BSplineCurve PolesCount=4 KnotsCount=2 Degree=3 IsPeriodic=0
    g74: BSplineCurve PolesCount=4 KnotsCount=2 Degree=3 IsPeriodic=0
    g75: BSplineCurve PolesCount=4 KnotsCount=2 Degree=3 IsPeriodic=0
    g76: BSplineCurve PolesCount=4 KnotsCount=2 Degree=3 IsPeriodic=0
    g77: BSplineCurve PolesCount=4 KnotsCount=2 Degree=3 IsPeriodic=0
    g78: BSplineCurve PolesCount=4 KnotsCount=2 Degree=3 IsPeriodic=0
    g79: BSplineCurve PolesCount=4 KnotsCount=2 Degree=3 IsPeriodic=0
    g80: BSplineCurve PolesCount=4 KnotsCount=2 Degree=3 IsPeriodic=0
    g81: BSplineCurve PolesCount=4 KnotsCount=2 Degree=3 IsPeriodic=0
    g82: BSplineCurve PolesCount=4 KnotsCount=2 Degree=3 IsPeriodic=0
    g83: BSplineCurve PolesCount=4 KnotsCount=2 Degree=3 IsPeriodic=0
    g84: BSplineCurve PolesCount=4 KnotsCount=2 Degree=3 IsPeriodic=0
    g85: BSplineCurve PolesCount=4 KnotsCount=2 Degree=3 IsPeriodic=0
    g86: BSplineCurve PolesCount=4 KnotsCount=2 Degree=3 IsPeriodic=0
    g87: BSplineCurve PolesCount=4 KnotsCount=2 Degree=3 IsPeriodic=0
    g88: BSplineCurve PolesCount=4 KnotsCount=2 Degree=3 IsPeriodic=0
    g89: BSplineCurve PolesCount=4 KnotsCount=2 Degree=3 IsPeriodic=0
    g90: BSplineCurve PolesCount=4 KnotsCount=2 Degree=3 IsPeriodic=0
    g91: BSplineCurve PolesCount=4 KnotsCount=2 Degree=3 IsPeriodic=0
    g92: BSplineCurve PolesCount=4 KnotsCount=2 Degree=3 IsPeriodic=0
    g93: BSplineCurve PolesCount=4 KnotsCount=2 Degree=3 IsPeriodic=0
    g94: BSplineCurve PolesCount=4 KnotsCount=2 Degree=3 IsPeriodic=0
    g95: BSplineCurve PolesCount=4 KnotsCount=2 Degree=3 IsPeriodic=0
    g96: BSplineCurve PolesCount=4 KnotsCount=2 Degree=3 IsPeriodic=0
    g97: BSplineCurve PolesCount=4 KnotsCount=2 Degree=3 IsPeriodic=0
    g98: BSplineCurve PolesCount=4 KnotsCount=2 Degree=3 IsPeriodic=0
    g99: BSplineCurve PolesCount=4 KnotsCount=2 Degree=3 IsPeriodic=0
    g100: BSplineCurve PolesCount=4 KnotsCount=2 Degree=3 IsPeriodic=0
    g101: BSplineCurve PolesCount=4 KnotsCount=2 Degree=3 IsPeriodic=0
    g102: BSplineCurve PolesCount=4 KnotsCount=2 Degree=3 IsPeriodic=0
    g103: BSplineCurve PolesCount=4 KnotsCount=2 Degree=3 IsPeriodic=0
    g104: BSplineCurve PolesCount=4 KnotsCount=2 Degree=3 IsPeriodic=0
    g105: BSplineCurve PolesCount=4 KnotsCount=2 Degree=3 IsPeriodic=0
    g106: BSplineCurve PolesCount=4 KnotsCount=2 Degree=3 IsPeriodic=0
    g107: BSplineCurve PolesCount=4 KnotsCount=2 Degree=3 IsPeriodic=0
    g108: BSplineCurve PolesCount=4 KnotsCount=2 Degree=3 IsPeriodic=0
    g109: BSplineCurve PolesCount=4 KnotsCount=2 Degree=3 IsPeriodic=0
    g110: BSplineCurve PolesCount=4 KnotsCount=2 Degree=3 IsPeriodic=0
    g111: BSplineCurve PolesCount=4 KnotsCount=2 Degree=3 IsPeriodic=0
    g112: BSplineCurve PolesCount=4 KnotsCount=2 Degree=3 IsPeriodic=0
    g113: BSplineCurve PolesCount=4 KnotsCount=2 Degree=3 IsPeriodic=0
    g114: BSplineCurve PolesCount=4 KnotsCount=2 Degree=3 IsPeriodic=0
    g115: BSplineCurve PolesCount=4 KnotsCount=2 Degree=3 IsPeriodic=0
    g116: BSplineCurve PolesCount=4 KnotsCount=2 Degree=3 IsPeriodic=0
    g117: BSplineCurve PolesCount=4 KnotsCount=2 Degree=3 IsPeriodic=0
    g118: BSplineCurve PolesCount=4 KnotsCount=2 Degree=3 IsPeriodic=0
    g119: BSplineCurve PolesCount=4 KnotsCount=2 Degree=3 IsPeriodic=0
    g120: BSplineCurve PolesCount=4 KnotsCount=2 Degree=3 IsPeriodic=0
    g121: BSplineCurve PolesCount=4 KnotsCount=2 Degree=3 IsPeriodic=0
    g122: BSplineCurve PolesCount=4 KnotsCount=2 Degree=3 IsPeriodic=0
    g123: BSplineCurve PolesCount=4 KnotsCount=2 Degree=3 IsPeriodic=0
    g124: BSplineCurve PolesCount=4 KnotsCount=2 Degree=3 IsPeriodic=0
    g125: BSplineCurve PolesCount=4 KnotsCount=2 Degree=3 IsPeriodic=0
    g126: BSplineCurve PolesCount=4 KnotsCount=2 Degree=3 IsPeriodic=0
    g127: BSplineCurve PolesCount=4 KnotsCount=2 Degree=3 IsPeriodic=0
    g128: BSplineCurve PolesCount=4 KnotsCount=2 Degree=3 IsPeriodic=0
    g129: BSplineCurve PolesCount=4 KnotsCount=2 Degree=3 IsPeriodic=0
    g130: BSplineCurve PolesCount=4 KnotsCount=2 Degree=3 IsPeriodic=0
    g131: BSplineCurve PolesCount=4 KnotsCount=2 Degree=3 IsPeriodic=0
    g132: BSplineCurve PolesCount=4 KnotsCount=2 Degree=3 IsPeriodic=0
    g133: BSplineCurve PolesCount=4 KnotsCount=2 Degree=3 IsPeriodic=0
    g134: BSplineCurve PolesCount=4 KnotsCount=2 Degree=3 IsPeriodic=0
    g135: BSplineCurve PolesCount=4 KnotsCount=2 Degree=3 IsPeriodic=0
    g136: BSplineCurve PolesCount=4 KnotsCount=2 Degree=3 IsPeriodic=0
    g137: BSplineCurve PolesCount=4 KnotsCount=2 Degree=3 IsPeriodic=0
    g138: BSplineCurve PolesCount=4 KnotsCount=2 Degree=3 IsPeriodic=0
    g139: BSplineCurve PolesCount=4 KnotsCount=2 Degree=3 IsPeriodic=0
    g140: BSplineCurve PolesCount=4 KnotsCount=2 Degree=3 IsPeriodic=0
    g141: BSplineCurve PolesCount=4 KnotsCount=2 Degree=3 IsPeriodic=0
    g142: BSplineCurve PolesCount=4 KnotsCount=2 Degree=3 IsPeriodic=0
    g143: BSplineCurve PolesCount=4 KnotsCount=2 Degree=3 IsPeriodic=0
    g144: BSplineCurve PolesCount=4 KnotsCount=2 Degree=3 IsPeriodic=0
    g145: BSplineCurve PolesCount=4 KnotsCount=2 Degree=3 IsPeriodic=0
    g146: BSplineCurve PolesCount=4 KnotsCount=2 Degree=3 IsPeriodic=0
    g147: BSplineCurve PolesCount=4 KnotsCount=2 Degree=3 IsPeriodic=0
    g148: BSplineCurve PolesCount=4 KnotsCount=2 Degree=3 IsPeriodic=0
    g149: BSplineCurve PolesCount=4 KnotsCount=2 Degree=3 IsPeriodic=0
    g150: BSplineCurve PolesCount=4 KnotsCount=2 Degree=3 IsPeriodic=0
    g151: BSplineCurve PolesCount=4 KnotsCount=2 Degree=3 IsPeriodic=0
    g152: BSplineCurve PolesCount=4 KnotsCount=2 Degree=3 IsPeriodic=0
    g153: BSplineCurve PolesCount=4 KnotsCount=2 Degree=3 IsPeriodic=0
    g154: BSplineCurve PolesCount=4 KnotsCount=2 Degree=3 IsPeriodic=0
    g155: BSplineCurve PolesCount=4 KnotsCount=2 Degree=3 IsPeriodic=0
    g156: BSplineCurve PolesCount=4 KnotsCount=2 Degree=3 IsPeriodic=0
    g157: BSplineCurve PolesCount=4 KnotsCount=2 Degree=3 IsPeriodic=0
    g158: BSplineCurve PolesCount=4 KnotsCount=2 Degree=3 IsPeriodic=0
    g159: BSplineCurve PolesCount=4 KnotsCount=2 Degree=3 IsPeriodic=0
    g160: BSplineCurve PolesCount=4 KnotsCount=2 Degree=3 IsPeriodic=0
    g161: BSplineCurve PolesCount=4 KnotsCount=2 Degree=3 IsPeriodic=0
    g162: BSplineCurve PolesCount=4 KnotsCount=2 Degree=3 IsPeriodic=0
    g163: BSplineCurve PolesCount=4 KnotsCount=2 Degree=3 IsPeriodic=0
    g164: BSplineCurve PolesCount=4 KnotsCount=2 Degree=3 IsPeriodic=0
    g165: BSplineCurve PolesCount=4 KnotsCount=2 Degree=3 IsPeriodic=0
    g166: BSplineCurve PolesCount=4 KnotsCount=2 Degree=3 IsPeriodic=0
    g167: BSplineCurve PolesCount=4 KnotsCount=2 Degree=3 IsPeriodic=0
    g168: BSplineCurve PolesCount=4 KnotsCount=2 Degree=3 IsPeriodic=0
    g169: BSplineCurve PolesCount=4 KnotsCount=2 Degree=3 IsPeriodic=0
    g170: BSplineCurve PolesCount=4 KnotsCount=2 Degree=3 IsPeriodic=0
    g171: BSplineCurve PolesCount=4 KnotsCount=2 Degree=3 IsPeriodic=0
    g172: BSplineCurve PolesCount=4 KnotsCount=2 Degree=3 IsPeriodic=0
    g173: BSplineCurve PolesCount=4 KnotsCount=2 Degree=3 IsPeriodic=0
    g174: BSplineCurve PolesCount=4 KnotsCount=2 Degree=3 IsPeriodic=0
    g175: BSplineCurve PolesCount=4 KnotsCount=2 Degree=3 IsPeriodic=0
  constraints (176):
    c: Coincident(g0,g1)
    c: Coincident(g1,g2)
    c: Coincident(g2,g3)
    c: Coincident(g3,g4)
    c: Coincident(g4,g5)
    c: Coincident(g5,g6)
    c: Coincident(g6,g7)
    c: Coincident(g7,g8)
    c: Coincident(g8,g9)
    c: Coincident(g9,g10)
    c: Coincident(g10,g11)
    c: Coincident(g11,g12)
    c: Coincident(g12,g13)
    c: Coincident(g13,g14)
    c: Coincident(g14,g0)
    c: Coincident(g15,g16)
    c: Coincident(g16,g17)
    c: Coincident(g17,g18)
    c: Coincident(g18,g19)
    c: Coincident(g19,g20)
    c: Coincident(g20,g21)
    c: Coincident(g21,g22)
    c: Coincident(g22,g23)
    c: Coincident(g23,g24)
    c: Coincident(g24,g25)
    c: Coincident(g25,g26)
    c: Coincident(g26,g27)
    c: Coincident(g27,g28)
    c: Coincident(g28,g29)
    c: Coincident(g29,g30)
    c: Coincident(g30,g31)
    c: Coincident(g31,g32)
    c: Coincident(g32,g15)
    c: Coincident(g33,g34)
    c: Coincident(g34,g35)
    c: Coincident(g35,g36)
    c: Coincident(g36,g37)
    c: Coincident(g37,g38)
    c: Coincident(g38,g39)
    c: Coincident(g39,g40)
    c: Coincident(g40,g41)
    c: Coincident(g41,g42)
    c: Coincident(g42,g43)
    c: Coincident(g43,g44)
    c: Coincident(g44,g45)
    c: Coincident(g45,g46)
    c: Coincident(g46,g47)
    c: Coincident(g47,g48)
    c: Coincident(g48,g49)
    c: Coincident(g49,g50)
    c: Coincident(g50,g51)
    c: Coincident(g51,g52)
    c: Coincident(g52,g53)
    c: Coincident(g53,g54)
    c: Coincident(g54,g55)
    c: Coincident(g55,g56)
    c: Coincident(g56,g57)
    c: Coincident(g57,g58)
    c: Coincident(g58,g59)
    c: Coincident(g59,g60)
    c: Coincident(g60,g61)
    c: Coincident(g61,g62)
    c: Coincident(g62,g63)
    c: Coincident(g63,g64)
    c: Coincident(g64,g65)
    c: Coincident(g65,g66)
    c: Coincident(g66,g67)
    c: Coincident(g67,g68)
    c: Coincident(g68,g69)
    c: Coincident(g69,g70)
    c: Coincident(g70,g71)
    c: Coincident(g71,g72)
    c: Coincident(g72,g73)
    c: Coincident(g73,g74)
    c: Coincident(g74,g75)
    c: Coincident(g75,g76)
    c: Coincident(g76,g77)
    c: Coincident(g77,g78)
    c: Coincident(g78,g79)
    c: Coincident(g79,g80)
    c: Coincident(g80,g81)
    c: Coincident(g81,g82)
    c: Coincident(g82,g83)
    c: Coincident(g83,g84)
    c: Coincident(g84,g85)
    c: Coincident(g85,g86)
    c: Coincident(g86,g87)
    c: Coincident(g87,g88)
    c: Coincident(g88,g89)
    c: Coincident(g89,g90)
    c: Coincident(g90,g91)
    c: Coincident(g91,g92)
    c: Coincident(g92,g93)
    c: Coincident(g93,g94)
    c: Coincident(g94,g95)
    c: Coincident(g95,g96)
    c: Coincident(g96,g97)
    c: Coincident(g97,g98)
    c: Coincident(g98,g99)
    c: Coincident(g99,g100)
    c: Coincident(g100,g101)
    c: Coincident(g101,g102)
    c: Coincident(g102,g33)
    c: Coincident(g103,g104)
    c: Coincident(g104,g105)
    c: Coincident(g105,g106)
    c: Coincident(g106,g107)
    c: Coincident(g107,g108)
    c: Coincident(g108,g109)
    c: Coincident(g109,g110)
    c: Coincident(g110,g111)
    c: Coincident(g111,g112)
    c: Coincident(g112,g113)
    c: Coincident(g113,g114)
    c: Coincident(g114,g115)
    c: Coincident(g115,g116)
    c: Coincident(g116,g117)
    c: Coincident(g117,g118)
    c: Coincident(g118,g119)
    c: Coincident(g119,g120)
    c: Coincident(g120,g121)
    c: Coincident(g121,g103)
    c: Coincident(g122,g123)
    c: Coincident(g123,g124)
    c: Coincident(g124,g125)
    c: Coincident(g125,g126)
    c: Coincident(g126,g127)
    c: Coincident(g127,g128)
    c: Coincident(g128,g129)
    c: Coincident(g129,g130)
    c: Coincident(g130,g131)
    c: Coincident(g131,g132)
    c: Coincident(g132,g133)
    c: Coincident(g133,g134)
    c: Coincident(g134,g135)
    c: Coincident(g135,g136)
    c: Coincident(g136,g137)
    c: Coincident(g137,g138)
    c: Coincident(g138,g139)
    c: Coincident(g139,g140)
    c: Coincident(g140,g141)
    c: Coincident(g141,g142)
    c: Coincident(g142,g143)
    c: Coincident(g143,g144)
    c: Coincident(g144,g122)
    c: Coincident(g145,g146)
    c: Coincident(g146,g147)
    c: Coincident(g147,g148)
    c: Coincident(g148,g149)
    c: Coincident(g149,g150)
    c: Coincident(g150,g151)
    c: Coincident(g151,g152)
    c: Coincident(g152,g153)
    c: Coincident(g153,g154)
    c: Coincident(g154,g155)
    c: Coincident(g155,g156)
    c: Coincident(g156,g157)
    c: Coincident(g157,g158)
    c: Coincident(g158,g159)
    c: Coincident(g159,g160)
    c: Coincident(g160,g145)
    c: Coincident(g161,g162)
    c: Coincident(g162,g163)
    c: Coincident(g163,g164)
    c: Coincident(g164,g165)
    c: Coincident(g165,g166)
    c: Coincident(g166,g167)
    c: Coincident(g167,g168)
    c: Coincident(g168,g169)
    c: Coincident(g169,g170)
    c: Coincident(g170,g171)
    c: Coincident(g171,g172)
    c: Coincident(g172,g173)
    c: Coincident(g173,g174)
    c: Coincident(g174,g175)
    c: Coincident(g175,g161)
FEATURE [PartDesign::Pocket] Pocket001
  BaseFeature = -> Pad007
  Direction = (0,1,-2e-16)
  Length = 5
  Length2 = 5
  Profile = -> Sketch010
  ReferenceAxis = -> Sketch010 [N_Axis]
  Refine = true
  Suppressed = false
  Type = 0
FEATURE [PartDesign::Pocket] Pocket002
  BaseFeature = -> Pocket001
  Direction = (0,1,-2e-16)
  Length = 5
  Length2 = 5
  Profile = -> Sketch011
  ReferenceAxis = -> Sketch011 [N_Axis]
  Refine = true
  Suppressed = false
  Type = 0
FEATURE [PartDesign::Body] Body002  label="phone holder"
  AllowCompound = false
  Group = -> [Sketch003,Pad003,Sketch004,Pad004,Sketch007,Pad006,Sketch009,Pad007,Sketch010,Sketch011,Pocket001,Pocket002]
  Origin = -> Origin002
  Placement = pos=(-40,-50,-5) rot=(0,0,1;0rad)
  Tip = -> Pocket002
FEATURE [Sketcher::SketchObject] Sketch012
  ArcFitTolerance = 1e-06
  AttachmentSupport = -> [Pocket]
  FullyConstrained = true
  MakeInternals = false
  MapMode = 5
  Placement = pos=(-40,0,0) rot=(0.707107,0,-0.707107;3.14159rad)
  sketch-geometry (1):
    g0: Circle CenterX=-30 CenterY=-26 CenterZ=0 NormalX=0 NormalY=0 NormalZ=1 AngleXU=0 Radius=3.1
  constraints (3):
    c: Diameter(g0) = 6.2
    c: Distance(g0,g-1) = 26
    c: DistanceX(g0,g-1) = 30
FEATURE [PartDesign::Pocket] Pocket003
  BaseFeature = -> Pocket
  Direction = (1,0,2e-16)
  Length = 10
  Length2 = 5
  Placement = pos=(0,0,0) rot=(1,0,0;1.5708rad)
  Profile = -> Sketch012
  ReferenceAxis = -> Sketch012 [N_Axis]
  Refine = true
  Suppressed = false
  Type = 0
FEATURE [Sketcher::SketchObject] Sketch013
  ArcFitTolerance = 1e-06
  AttachmentSupport = -> [Pocket003]
  FullyConstrained = true
  MakeInternals = false
  MapMode = 5
  Placement = pos=(0,8.4e-15,0) rot=(-1,0,0;1.5708rad)
  sketch-geometry (8):
    g0: LineSegment StartX=17.5 StartY=-66 StartZ=0 EndX=17.5 EndY=-10 EndZ=0
    g1: LineSegment StartX=17.5 StartY=-10 StartZ=0 EndX=-17.5 EndY=-10 EndZ=0
    g2: LineSegment StartX=-17.5 StartY=-10 StartZ=0 EndX=-17.5 EndY=-66 EndZ=0
    g3: LineSegment StartX=-17.5 StartY=-66 StartZ=0 EndX=17.5 EndY=-66 EndZ=0
    g4: LineSegment StartX=15 StartY=-64 StartZ=0 EndX=15 EndY=-12 EndZ=0
    g5: LineSegment StartX=15 StartY=-12 StartZ=0 EndX=-15 EndY=-12 EndZ=0
    g6: LineSegment StartX=-15 StartY=-12 StartZ=0 EndX=-15 EndY=-64 EndZ=0
    g7: LineSegment StartX=-15 StartY=-64 StartZ=0 EndX=15 EndY=-64 EndZ=0
  constraints (24):
    c: Coincident(g0,g1)
    c: Coincident(g1,g2)
    c: Coincident(g2,g3)
    c: Coincident(g3,g0)
    c: Vertical(g0)
    c: Vertical(g2)
    c: Horizontal(g1)
    c: Horizontal(g3)
    c: Distance(g0,g2) = 35
    c: Distance(g1,g3) = 56
    c: Coincident(g4,g5)
    c: Coincident(g5,g6)
    c: Coincident(g6,g7)
    c: Coincident(g7,g4)
    c: Vertical(g4)
    c: Vertical(g6)
    c: Horizontal(g5)
    c: Horizontal(g7)
    c: Distance(g4,g6) = 30
    c: Distance(g5,g7) = 52
    c: Distance(g0,g-2) = 17.5
    c: Distance(g4,g-2) = 15
    c: Distance(g0,g-1) = 10
    c: Distance(g4,g-1) = 12
FEATURE [PartDesign::Pad] Pad008
  BaseFeature = -> Pocket003
  Direction = (0,1,2e-16)
  Length = 3
  Length2 = 10
  Placement = pos=(0,0,0) rot=(1,0,0;1.5708rad)
  Profile = -> Sketch013
  ReferenceAxis = -> Sketch013 [N_Axis]
  Refine = true
  Suppressed = false
  Type = 0
FEATURE [PartDesign::Body] Body  label="Power button case"
  AllowCompound = false
  Group = -> [Sketch,Pad,Sketch001,Pad001,Sketch005,Pad005,Sketch008,Pocket,Sketch012,Pocket003,Sketch013,Pad008]
  Origin = -> Origin
  Placement = pos=(0,-43,0) rot=(0,0,1;0rad)
  Tip = -> Pad008
